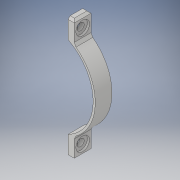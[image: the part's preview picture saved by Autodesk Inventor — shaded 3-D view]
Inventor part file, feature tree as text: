
AUTODESK INVENTOR PART (.ipt)
format: ipt  version: 2019 (Build 230136000, 136)  size: 145,408 bytes
history: native  units: mm
features: sketch x2, extrude x1, hole x1, chamfer x1, mirror x1, projected_geometry x1
ambient origin geometry x8: Origin, YZ Plane, XZ Plane, XY Plane, X Axis, Y Axis, Z Axis, Center Point
bodies: Solide1 (feature_tree)
feature tree (7):
  extrude  "Extrusion1"  Depth=1.0mm
  hole  "Perçage1"  [1 undecoded]
  chamfer  "Chanfrein1"  Distance=10.0mm
  mirror  "Symétrie1"
  sketch  "Esquisse1"
  sketch  "Esquisse2"
  projected_geometry  "Boucle projetée1"
note: 1 required parameter value undecoded (feature->parameter linkage not recoverable at this tier; creation-order binding heuristic only, values carry confidence <= 0.55)
